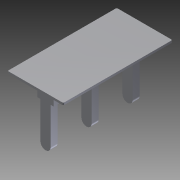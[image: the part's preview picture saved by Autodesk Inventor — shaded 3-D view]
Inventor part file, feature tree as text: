
AUTODESK INVENTOR PART (.ipt)
format: ipt  version: 2011 SP1 (Build 150282100, 282)  size: 115,200 bytes
history: native  units: in
note: dims shown in document units (in); Inventor stores cm internally (conversion verified against a paired STEP export)
features: other x7, extrude x2, sketch x2, pattern_linear x1
ambient origin geometry x8: Origin, YZ Plane, XZ Plane, XY Plane, X Axis, Y Axis, Z Axis, Center Point
bodies: Solid1 (feature_tree)
feature tree (12):
  extrude  "Extrusion1"  Depth=0.031in TaperAngle=0.0deg
  extrude  "Extrusion2"  [1 undecoded]
  pattern_linear  "Rectangular Pattern1"  [2 undecoded]
  other  "to_base_XY"
  other  "to_base_YZ"
  other  "to_base_ZX"
  other  "to_base_X"
  other  "to_base_Y"
  other  "to_base_Z"
  other  "to_base_Center"
  sketch  "Sketch_2"  dims[d0=0.01in d1=0.0in d2=0.031in d3=0.0in]
  sketch  "Sketch_7"  dims[d4=1.1811in d6=0.185in d7=0.3937in d9=0.0in]
note: 3 required parameter values undecoded (feature->parameter linkage not recoverable at this tier; creation-order binding heuristic only, values carry confidence <= 0.55)
